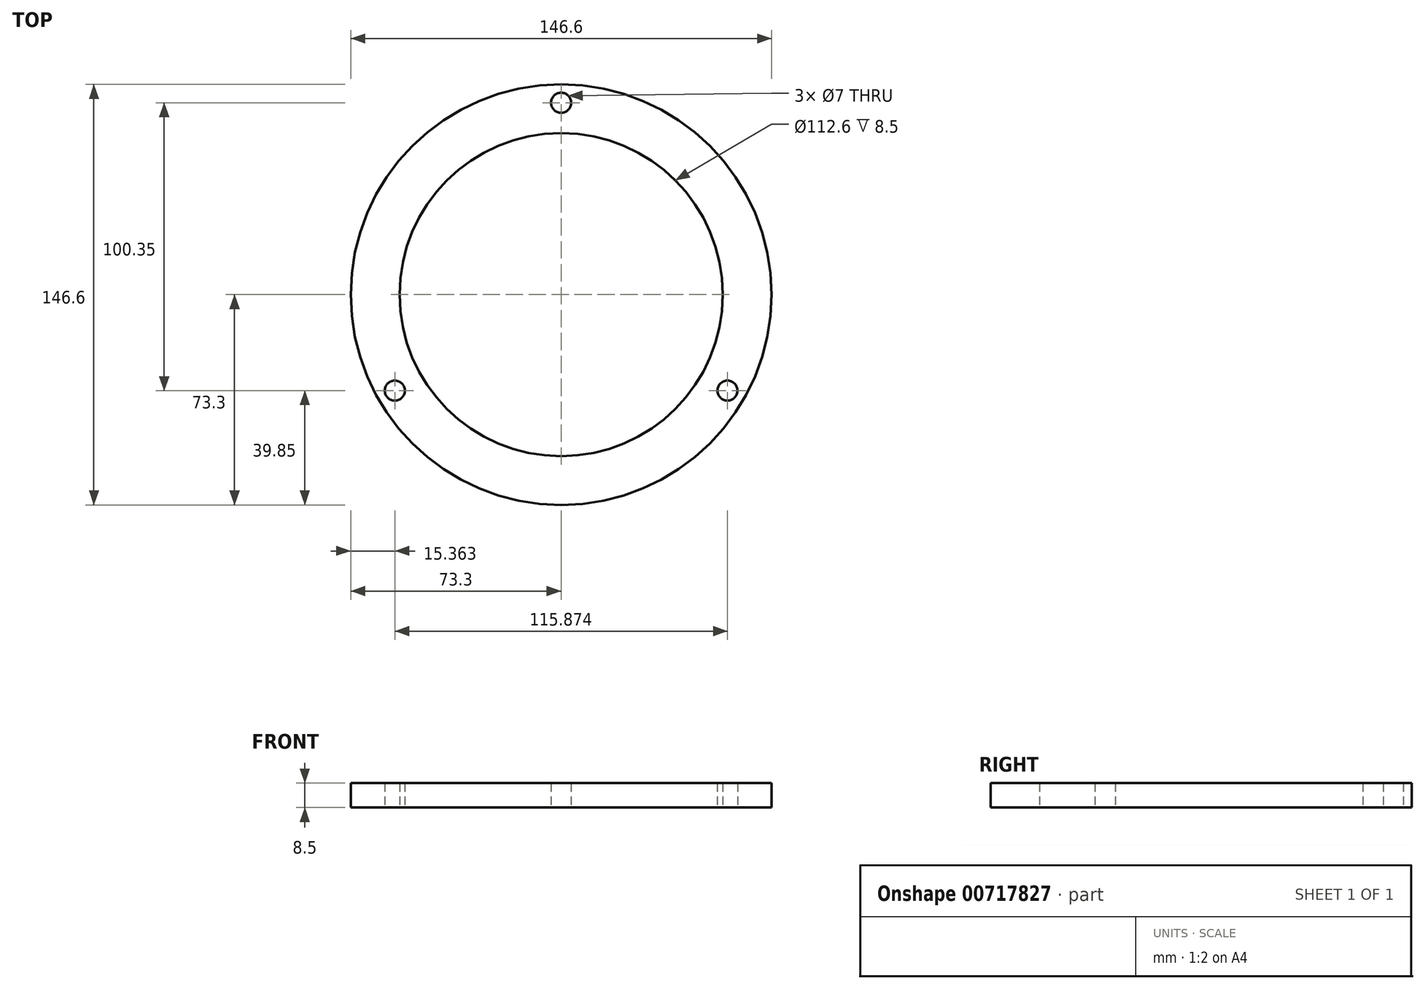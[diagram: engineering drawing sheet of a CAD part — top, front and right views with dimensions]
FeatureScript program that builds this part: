
annotation { "Feature Type Name" : "Feature", "Feature Type Description" : "" }
export const myFeature = defineFeature(function(context is Context, id is Id, definition is map)
    precondition{}
    {
        {
            var Q0;
            Q0=qCreatedBy(makeId("Top.planeOp"),FACE);
            var sketch = newSketch(context, id + "F0", { "sketchPlane" : qUnion([Q0])});
            skCircle(sketch, "E0", {"center": v(0, 0) * mm, "radius": 73.3 * mm});
            skCircle(sketch, "E1.0", {"center": v(0, 0) * mm, "radius": 56.3 * mm});
            skCircle(sketch, "E2", {"center": v(0, 66.9) * mm, "radius": 3.5 * mm});
            skCircle(sketch, "E3.1.0", {"center": v(-57.94, -33.45) * mm, "radius": 3.5 * mm});
            skCircle(sketch, "E3.2.0", {"center": v(57.94, -33.45) * mm, "radius": 3.5 * mm});
            skSolve(sketch);
        }
        {
            var Q0;
            Q0=makeQuery(id+"F0.imprint","IMPRINT",FACE,{"disambiguationData":[TD([[makeQuery(id+"F0.imprint","IMPRINT",EDGE,{"derivedFrom":sQuery(id+"F0.wireOp",EDGE,"E0")}),1.0]])]});
            extrude(context, id + "F1", {"entities" : qUnion([Q0]), "depth" : 8.5 * mm, "offsetDistance" : 25 * mm});
        }
    });
